# Revit family: GAHP GS_en
name_source: partatom
category: Modelli generici
revit_build: Autodesk Revit 2017 (Build: 20160225_1515(x64)
units: mm (PartAtom-declared; Revit-internal decimal feet)

## family parameters
Basato su piano di lavoro = No
Condiviso = No
Punto di calcolo locali = No
Può ospitare armatura = No
Quota connettore circolare = Usa diametro
Sempre verticale = Sì
Taglio con vuoti quando caricato = No
Tipo di parte = Normale

## types (1)
- GAHP GS
    A01.Seasonal space heating energy efficiency class (ErP) - medium-temperature application (55 °C) = A++
    A02.Seasonal space heating energy efficiency class (ErP) - low-temperature application (35 °C) = A+
    A03.Heat output - Evaporator inlet temperature/Delivery temperature - B0W35 = 41600
    A04.Heat output - Evaporator inlet temperature/Delivery temperature - B0W50 = 37600
    A05.Heat output - Evaporator inlet temperature/Delivery temperature - B0W65 = 31400
    A09.GUE efficiency - Evaporator inlet temperature/Delivery temperature - B0W35 = 165.00%
    A10.GUE efficiency - Evaporator inlet temperature/Delivery temperature - B0W50 = 149.00%
    A11.GUE efficiency - Evaporator inlet temperature/Delivery temperature - B0W65 = 125.00%
    A15.Heat input - nominal (1013 bar - 15°C) = 25700 W
    A16.Heat input - real = 25200 W
    A17.Hot water delivery temperature - maximum for heating = 65 °C
    A18.Hot water delivery temperature - maximum for DHW = 70 °C
    A19.Hot water return temperature - maximum for heating = 55 °C
    A20.Hot water return temperature - maximum for DHW = 60 °C
    A21.Hot water return temperature - minimum in continuous operation = 30 °C
    A22.Thermal differential - nominal = 10 °C
    A23.Heating water flow - nominal = 3.2 m³/h
    A24.Heating water flow - maximum = 4.0 m³/h
    A25.Heating water flow - minimum = 1.4 m³/h
    A26.Pressure drop heating mode - for nominal water flow (B0W50) = 0.5 barra
    A27.Pressure drop heating mode - for nominal water flow rate (W10W50) = 0.0 barra
    A28.Ambient air temperature (dry bulb) - maximum = 45 °C
    A29.Ambient air temperature (dry bulb) - minimum = 0 °C
    A30.Power recovered from renewable source - Evaporator inlet temperature/Delivery temperature - B0W35 = 16400 W
    A31.Power recovered from renewable source - Evaporator inlet temperature/Delivery temperature - B0W50 = 12100 W
    A32.Power recovered from renewable source - Evaporator inlet temperature/Delivery temperature - B0W65 = 7000 W
    A36.Renewable source water return temperature - maximum = 45 °C
    A37.Renewable source delivery water temperature - minimum = -5 °C
    A38.Renewable source water flow rate (with 25% glycol) - nominal (B0W50) = 3.0 m³/h
    A39.Renewable source water flow rate (with 25% glycol) - maximum = 4.0 m³/h
    A40.Renewable source water flow rate (with 25% glycol) - minimum = 2.0 m³/h
    A44.Renewable source water flow rate - at nominal water flow = 0.5 barra
    B01.Power supply - voltage = 230 V
    B02.Power supply - type = single phase
    B03.Power supply - frequency = 50 Hz
    B04.Electrical power absorption - nominal = 410 W
    B05.Degree of protection - IP = X5D
    BIMobject category = Other HVAC
    BIMobject category code = hvac-other
    BIMobject main category = HVAC
    BIMobject main category code = hvac
    Brand url = https://www.robur.com
    C01.Gas consumption - G20 natural gas (nominal) = 2.7 m³/h
    C02.Gas consumption - G20 natural gas (minimum) = 1.3 m³/h
    C03.Gas consumption - G25 (nominal) = 3.2 m³/h
    C04.Gas consumption - G25 (minimum) = 1.6 m³/h
    C05.Gas consumption - G30 (nominal) [kg/h] = 2.03
    C06.Gas consumption - G30 (minimum) [kg/h] = 0.99
    C07.Gas consumption - G31 (nominal) [kg/h] = 2
    C08.Gas consumption - G31 (minimum) [kg/h] = 0.98
    C09.NOx emission class = 5
    C10.NOx emission[ppm] = 25
    C11.CO emission [ppm] = 36
    C12.Sound power Lw (maximum) - [dB(A)] = 66.1
    C13.Sound pressure Lp at 5 m (maximum) - [dB(A)] = 44.1
    C14.Minimum storage temperature = -30 °C
    C15.Maximum water pressure in operation = 4.0 barra
    C16.Maximum flow flue condensate = 0.0 m³/h
    C17.Water content inside the apparatus - hot side = 4.0 L
    C18.Water content inside the apparatus - cold side = 3.0 L
    C19.Water fitting - type = F
    C20.Water fitting - thread = 1 1/4"
    C21.Gas connection - type = F
    C22.Gas connection - thread = 3/4"
    C23.Safety valve outlet channel fiting = 1 1/4"
    C24.Flue gas exhaust - diameter = 80.00 mm
    C25.Flue gas exhaust - residual head = 80.0 Pa
    C26.Flue gas exhaust - product configuration = C63
    C27.Type of installation = C13, C33, C43, C53, C63, C83, B23P, B33
    C28.Dimensions - width = 848.00 mm
    C29.Dimensions - depth = 690.00 mm
    C30.Dimensions - height = 1278.00 mm
    C31.Weight - in operation = 300.00 kg
    D01.Cooling fluid - ammonia R717 = 7.00 kg
    D02.Cooling fluid - water = 10.00 kg
    D03.Maximum pressure of the cooling circuit = 32.0 barra
    Date of publishing = 7/24/2018
    Design country = Italy
    E01.Components under pressure - generator = 18.6 L
    E02.Components under pressure - leveling chamber = 11.5 L
    E03.Components under pressure - evaporator = 3.7 L
    E04.Components under pressure - cooling volume transformer = 4.5 L
    E05.Components under pressure - absorber/condenser = 3.7 L
    E06.Components under pressure - cooling absorber solution = 6.3 L
    E07.Components under pressure - silution pump = 3.3 L
    E08.test pressure (in air) [bar g] = 55
    E09.Maximum pressure of the cooling circuit [bar g] = 32
    E10.Filling ratio [kg NH3/l] = 0.146
    E11.Fluid group = 1°
    Edition number = 1
    Installation instructions = https://www.robur.com
    Manufacturer country = Italy
    Manufacturer name = Robur
    Masterformat 2014 Code = 48 16 13
    Masterformat 2014 Description = Geothermal Energy Heat Pumps
    Material main = Steel
    Material secondary = Plastic
    NBS Reference Code = 68-38
    NBS Reference Description = Heat Pumps
    Nominal height = 1278 mm  [stored 4.19291 ft]
    Nominal width = 848 mm  [stored 2.78215 ft]
    OmniClass Code = 23-33 17 00
    OmniClass Description = Heat Pumps
    Product Guid = f3b294b3-e44a-43aa-88ce-942e4e55177a
    Product SKU = gahp-gs
    Product certification = https://www.robur.com
    Product data url = https://bimobject.com
    Product family = Heat Pumps
    Product group = Heating
    Product url = https://www.robur.com
    QR code = http://bimobject.com
    Technical description = https://www.robur.com
    UNSPSC Code = 40101806
    Uniclass 1.4 Code = L7524
    Uniclass 1.4 Description = Heat pumps
    Uniclass 2.0 Code = PR-68-38
    Uniclass 2.0 Description = Heat Pumps
    Uniclass 2015 Code = Pr_70_60_37
    Uniclass 2015 Name = Heat pumps
    Uniformat II Code = D3020
    Uniformat II Description = Heat Generating Systems
    Weight Net (Kg) = 300
    Youtube clip = https://www.youtube.com

note: source unit labels omitted for A03.Heat output - Evaporator inlet temperature/Delivery temperature - B0W35, A04.Heat output - Evaporator inlet temperature/Delivery temperature - B0W50, A05.Heat output - Evaporator inlet temperature/Delivery temperature - B0W65 — the stored unit's dimension contradicts the parameter name (converter mislabeling)

note: [stored X ft] marks values corroborated as IEEE doubles in the binary element streams (Revit-internal decimal feet)
